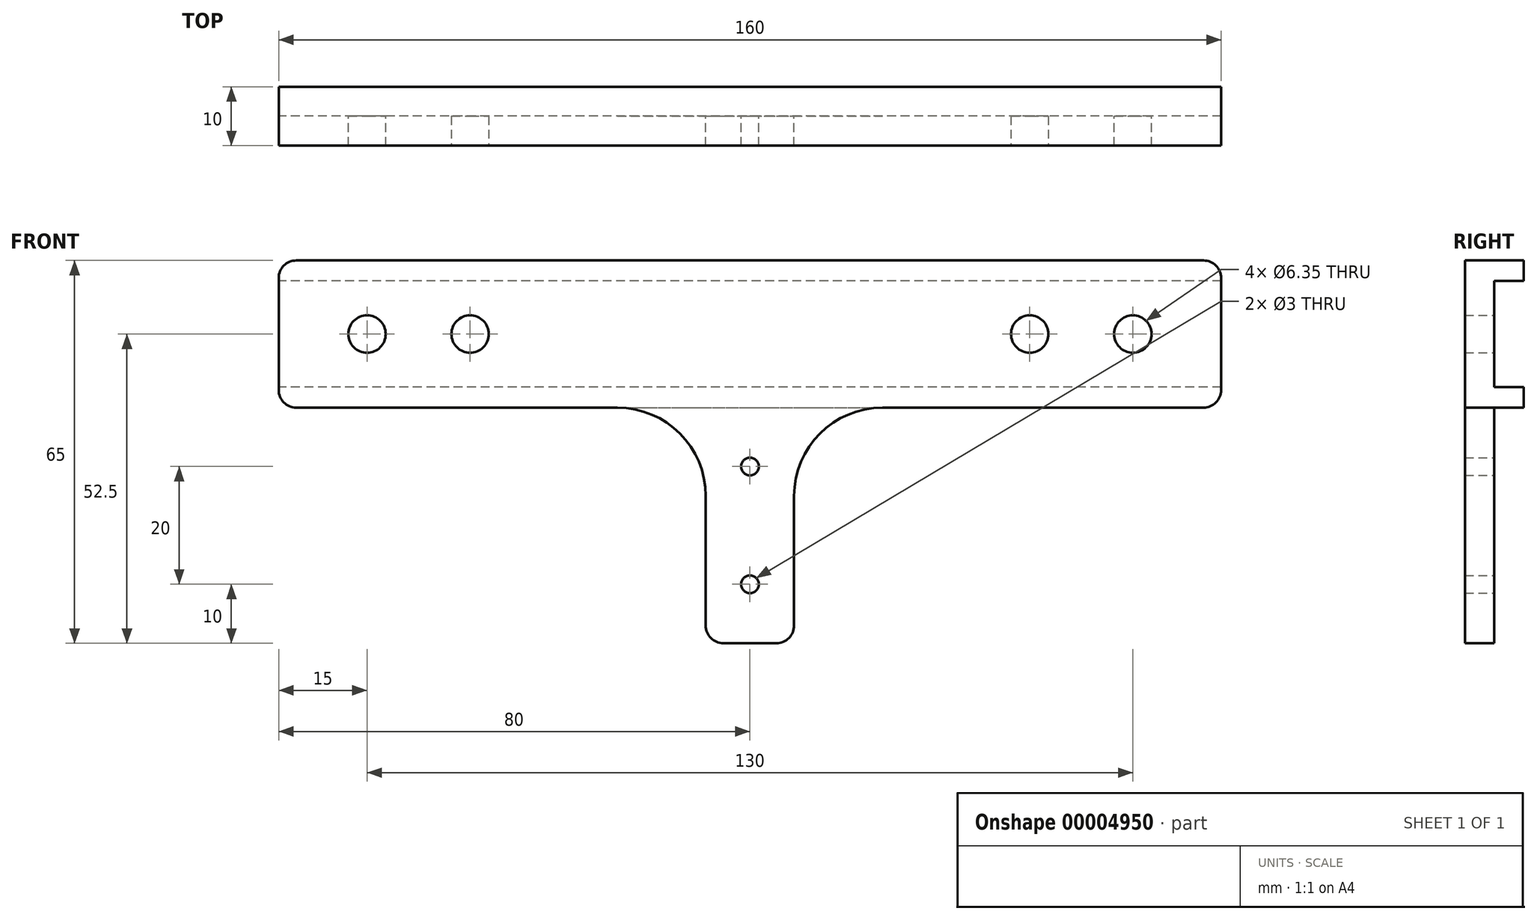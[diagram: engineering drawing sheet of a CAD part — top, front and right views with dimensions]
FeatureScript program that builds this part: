
annotation { "Feature Type Name" : "Feature", "Feature Type Description" : "" }
export const myFeature = defineFeature(function(context is Context, id is Id, definition is map)
    precondition{}
    {
        {
            var Q0;
            Q0=qCreatedBy(makeId("Front.planeOp"),FACE);
            var sketch = newSketch(context, id + "F0", { "sketchPlane" : qUnion([Q0])});
            skLineSegment(sketch, "E0", {"start": v(0, 0) * mm, "end": v(0, 31.45) * mm, "construction": true});
            skCircle(sketch, "E1", {"center": v(0, 0) * mm, "radius": 1.5 * mm});
            skCircle(sketch, "E2", {"center": v(0, 20) * mm, "radius": 1.5 * mm});
            skLineSegment(sketch, "E3", {"start": v(-7.5, -10) * mm, "end": v(7.5, -10) * mm});
            skPoint(sketch, "E4", {"position": v(0, -10) * mm});
            skLineSegment(sketch, "E5", {"start": v(-7.5, -10) * mm, "end": v(-7.5, 30) * mm});
            skLineSegment(sketch, "E6", {"start": v(-7.5, 30) * mm, "end": v(-80, 30) * mm});
            skLineSegment(sketch, "E7", {"start": v(-80, 30) * mm, "end": v(-80, 55) * mm});
            skLineSegment(sketch, "E8.0.MirrorCS", {"start": v(7.5, -10) * mm, "end": v(7.5, 30) * mm});
            skLineSegment(sketch, "E8.1.MirrorCS", {"start": v(7.5, 30) * mm, "end": v(80, 30) * mm});
            skLineSegment(sketch, "E8.2.MirrorCS", {"start": v(80, 30) * mm, "end": v(80, 55) * mm});
            skLineSegment(sketch, "E9", {"start": v(-80, 55) * mm, "end": v(80, 55) * mm});
            skLineSegment(sketch, "E10", {"start": v(-80, 42.5) * mm, "end": v(80, 42.5) * mm, "construction": true});
            skCircle(sketch, "E11", {"center": v(-65, 42.5) * mm, "radius": 3.17 * mm});
            skCircle(sketch, "E12.0.MirrorC", {"center": v(65, 42.5) * mm, "radius": 3.17 * mm});
            skSolve(sketch);
        }
        {
            var Q0;
            Q0 = qSketchRegion(id + "F0", true);
            extrude(context, id + "F1", {"entities" : qUnion([Q0]), "depth" : 5 * mm, "symmetric" : true});
        }
        {
            var Q0;
            Q0=makeQuery(id+"F1.opExtrude","CAP_FACE",FACE,{"disambiguationData":[OSD([sQuery(id+"F0.wireOp",EDGE,"E1"),sQuery(id+"F0.wireOp",EDGE,"E2"),sQuery(id+"F0.wireOp",EDGE,"E3"),sQuery(id+"F0.wireOp",EDGE,"E5"),sQuery(id+"F0.wireOp",EDGE,"E6"),sQuery(id+"F0.wireOp",EDGE,"E7"),sQuery(id+"F0.wireOp",EDGE,"E8.0.MirrorCS"),sQuery(id+"F0.wireOp",EDGE,"E8.1.MirrorCS"),sQuery(id+"F0.wireOp",EDGE,"E8.2.MirrorCS"),sQuery(id+"F0.wireOp",EDGE,"E9"),sQuery(id+"F0.wireOp",EDGE,"E11"),sQuery(id+"F0.wireOp",EDGE,"E12.0.MirrorC")])],"isStart":true});
            var sketch = newSketch(context, id + "F2", { "sketchPlane" : qUnion([Q0])});
            skLineSegment(sketch, "E13.bottom", {"start": v(-80, 55) * mm, "end": v(80, 55) * mm});
            skLineSegment(sketch, "E13.top", {"start": v(-80, 51.5) * mm, "end": v(80, 51.5) * mm});
            skLineSegment(sketch, "E13.left", {"start": v(-80, 55) * mm, "end": v(-80, 51.5) * mm});
            skLineSegment(sketch, "E13.right", {"start": v(80, 55) * mm, "end": v(80, 51.5) * mm});
            skLineSegment(sketch, "E14.bottom", {"start": v(-80, 30) * mm, "end": v(80, 30) * mm});
            skLineSegment(sketch, "E14.top", {"start": v(-80, 33.5) * mm, "end": v(80, 33.5) * mm});
            skLineSegment(sketch, "E14.left", {"start": v(-80, 30) * mm, "end": v(-80, 33.5) * mm});
            skLineSegment(sketch, "E14.right", {"start": v(80, 30) * mm, "end": v(80, 33.5) * mm});
            skSolve(sketch);
        }
        {
            var Q0;
            Q0 = qSketchRegion(id + "F2", true);
            extrude(context, id + "F3", {"entities" : qUnion([Q0]), "operationType" : NewBodyOperationType.ADD, "depth" : 5 * mm});
        }
        {
            var Q0;
            Q0=makeQuery(id+"F3.boolean.opBoolean","MERGE",EDGE,{"derivedFrom":[makeQuery(id+"F1.opExtrude","SWEPT_EDGE",EDGE,{"disambiguationData":[OSD([sQuery(id+"F0.wireOp",EDGE,"E8.2.MirrorCS"),sQuery(id+"F0.wireOp",EDGE,"E9")])]}),makeQuery(id+"F3.opExtrude","SWEPT_EDGE",EDGE,{"disambiguationData":[OSD([sQuery(id+"F2.wireOp",EDGE,"E13.bottom"),sQuery(id+"F2.wireOp",EDGE,"E13.left")])]})]});
            var Q1;
            Q1=makeQuery(id+"F3.boolean.opBoolean","MERGE",EDGE,{"derivedFrom":[makeQuery(id+"F1.opExtrude","SWEPT_EDGE",EDGE,{"disambiguationData":[OSD([sQuery(id+"F0.wireOp",EDGE,"E8.1.MirrorCS"),sQuery(id+"F0.wireOp",EDGE,"E8.2.MirrorCS")])]}),makeQuery(id+"F3.opExtrude","SWEPT_EDGE",EDGE,{"disambiguationData":[OSD([sQuery(id+"F2.wireOp",EDGE,"E14.bottom"),sQuery(id+"F2.wireOp",EDGE,"E14.left")])]})]});
            var Q2;
            Q2=makeQuery(id+"F3.boolean.opBoolean","MERGE",EDGE,{"derivedFrom":[makeQuery(id+"F1.opExtrude","SWEPT_EDGE",EDGE,{"disambiguationData":[OSD([sQuery(id+"F0.wireOp",EDGE,"E6"),sQuery(id+"F0.wireOp",EDGE,"E7")])]}),makeQuery(id+"F3.opExtrude","SWEPT_EDGE",EDGE,{"disambiguationData":[OSD([sQuery(id+"F2.wireOp",EDGE,"E14.bottom"),sQuery(id+"F2.wireOp",EDGE,"E14.right")])]})]});
            var Q3;
            Q3=makeQuery(id+"F3.boolean.opBoolean","MERGE",EDGE,{"derivedFrom":[makeQuery(id+"F1.opExtrude","SWEPT_EDGE",EDGE,{"disambiguationData":[OSD([sQuery(id+"F0.wireOp",EDGE,"E7"),sQuery(id+"F0.wireOp",EDGE,"E9")])]}),makeQuery(id+"F3.opExtrude","SWEPT_EDGE",EDGE,{"disambiguationData":[OSD([sQuery(id+"F2.wireOp",EDGE,"E13.bottom"),sQuery(id+"F2.wireOp",EDGE,"E13.right")])]})]});
            var Q4;
            Q4=makeQuery(id+"F3.opExtrude","CAP_EDGE",EDGE,{"disambiguationData":[OSD([sQuery(id+"F2.wireOp",EDGE,"E13.top")])],"isStart":true});
            var Q5;
            Q5=makeQuery(id+"F3.opExtrude","CAP_EDGE",EDGE,{"disambiguationData":[OSD([sQuery(id+"F2.wireOp",EDGE,"E14.top")])],"isStart":true});
            var Q6;
            Q6=makeQuery(id+"F1.opExtrude","SWEPT_EDGE",EDGE,{"disambiguationData":[OSD([sQuery(id+"F0.wireOp",EDGE,"E3"),sQuery(id+"F0.wireOp",EDGE,"E8.0.MirrorCS")])]});
            var Q7;
            Q7=makeQuery(id+"F1.opExtrude","SWEPT_EDGE",EDGE,{"disambiguationData":[OSD([sQuery(id+"F0.wireOp",EDGE,"E3"),sQuery(id+"F0.wireOp",EDGE,"E5")])]});
            fillet(context, id + "F4", {"entities" : qUnion([Q0, Q1, Q2, Q3, Q4, Q5, Q6, Q7]), "radius" : 3 * mm, "tangentPropagation" : true, "allowEdgeOverflow" : false});
        }
        {
            var Q0;
            Q0=makeQuery(id+"F1.opExtrude","CAP_FACE",FACE,{"disambiguationData":[OSD([sQuery(id+"F0.wireOp",EDGE,"E1"),sQuery(id+"F0.wireOp",EDGE,"E2"),sQuery(id+"F0.wireOp",EDGE,"E3"),sQuery(id+"F0.wireOp",EDGE,"E5"),sQuery(id+"F0.wireOp",EDGE,"E6"),sQuery(id+"F0.wireOp",EDGE,"E7"),sQuery(id+"F0.wireOp",EDGE,"E8.0.MirrorCS"),sQuery(id+"F0.wireOp",EDGE,"E8.1.MirrorCS"),sQuery(id+"F0.wireOp",EDGE,"E8.2.MirrorCS"),sQuery(id+"F0.wireOp",EDGE,"E9"),sQuery(id+"F0.wireOp",EDGE,"E11"),sQuery(id+"F0.wireOp",EDGE,"E12.0.MirrorC")])],"isStart":false});
            var sketch = newSketch(context, id + "F5", { "sketchPlane" : qUnion([Q0])});
            skLineSegment(sketch, "E15", {"start": v(-65, 42.5) * mm, "end": v(65, 42.5) * mm, "construction": true});
            skLineSegment(sketch, "E16", {"start": v(0, 42.5) * mm, "end": v(0, 55) * mm, "construction": true});
            skCircle(sketch, "E17", {"center": v(-47.5, 42.5) * mm, "radius": 3.17 * mm});
            skCircle(sketch, "E18.0.MirrorC", {"center": v(47.5, 42.5) * mm, "radius": 3.17 * mm});
            skSolve(sketch);
        }
        {
            var Q0;
            Q0 = qSketchRegion(id + "F5", true);
            extrude(context, id + "F6", {"entities" : qUnion([Q0]), "operationType" : NewBodyOperationType.REMOVE, "oppositeDirection" : true, "depth" : 25 * mm});
        }
        {
            var Q0;
            Q0=makeQuery(id+"F1.opExtrude","SWEPT_EDGE",EDGE,{"disambiguationData":[OSD([sQuery(id+"F0.wireOp",EDGE,"E8.0.MirrorCS"),sQuery(id+"F0.wireOp",EDGE,"E8.1.MirrorCS")])]});
            var Q1;
            Q1=makeQuery(id+"F1.opExtrude","SWEPT_EDGE",EDGE,{"disambiguationData":[OSD([sQuery(id+"F0.wireOp",EDGE,"E5"),sQuery(id+"F0.wireOp",EDGE,"E6")])]});
            fillet(context, id + "F7", {"entities" : qUnion([Q0, Q1]), "radius" : 15 * mm, "tangentPropagation" : true, "allowEdgeOverflow" : false});
        }
    });
